# Revit family: Metal_Lockers-Salsbury_Industries-51000_Series-3_Wide_Units
name_source: partatom
category: Specialty Equipment
units: mm (PartAtom-declared; Revit-internal decimal feet)

## family parameters
Always vertical = Yes
Classification Number = 23.40.00.00
Cut with Voids When Loaded = No
Enable Cutting in Views = No
Maintain Annotation Orientation = No
Part Type = Normal
Room Calculation Point = No
Round Connector Dimension = Use Diameter
Shared = No
Work Plane-Based = No

## types (6) — shared parameters
Assembly Code = C1030310
Building Codes = https://www.lockers.com
Construction Details = https://www.lockers.com
Door Location D1 = Metal Locker Doors-15 inch with Hasps : Single Tier Door - 6 foot
Green Building-LEED = https://www.arcat.com
Hasp Handle Material = Plastic - Salsbury Finish - Black
Hasp Plate Rivet Material = Steel -Salsbury Finish - Polished Steel
Installation-Fabrication = https://www.lockers.com
Keynote = 10 51 00
Manufacturer = Salsbury Industries
Manufacturer Fax = 1-800-562-5399
Manufacturer Website = https://www.lockers.com
MasterFormat Number = 10 51 13
MasterFormat Title = Lockers
OmniClass 23 Number = 23.40.00.00
OmniClass 23 Title = Equipment and Furnishings
Product Data = https://www.lockers.com
Revision = R1_2018-10
Sales Information = https://www.lockers.com
Specification = https://www.lockers.com
Test Data = https://www.lockers.com
Type Comments = 15" Wide Standard Metal Lockers - Single Tier
URL = www.lockers.com
Unit Height = 72 "
Version = 2.0 (02/28/18)
Width = 45.04 "
zero-valued in all types: Default Elevation

## per-type parameters (varying)
| type | Base Height | Depth | Description | Model | Sloping Hood Height | Standard Leg Base | Zee Base |
| 51365 - with Standard 6" High Legs | 6 " | 15.01 " | 3 Wide - 6 Feet High - 15 Inches Deep | 51365 | 8.682 " | Metal Locker Legs - 3 Wide : 6" High - 45"W x 15"D | Metal Locker Zee Base - 3 Wide : None |
| 51368 - with Standard 6" High Legs | 6 " | 18.01 " | 3 Wide - 6 Feet High - 18 Inches Deep | 51368 | 10.739 " | Metal Locker Legs - 3 Wide : 6" High - 45"W x 18"D | Metal Locker Zee Base - 3 Wide : None |
| 51365 - with 77575 Zee Base and 77550 Lockers without Legs | 4 " | 15.01 " | 3 Wide - 6 Feet High - 15 Inches Deep with Zee Base and Lockers without Legs | 51365 with 77575 and 77550 | 8.682 " | Metal Locker Legs - 3 Wide : No Legs | Metal Locker Zee Base - 3 Wide : 77575 - 45"W x 15"D |
| 51368 - with 77578 Zee Base and 77550 Lockers without Legs | 4 " | 18.01 " | 3 Wide - 6 Feet High - 18 Inches Deep with Zee Base and Lockers without Legs | 51368 with 77578 and 77550 | 10.739 " | Metal Locker Legs - 3 Wide : No Legs | Metal Locker Zee Base - 3 Wide : 77578 - 45"W x 18"D |
| 51365 - with 77550 Lockers without Legs | 0 " | 15.01 " | 3 Wide - 6 Feet High - 15 Inches Deep with Lockers without Legs | 51365 with 77550 | 8.682 " | Metal Locker Legs - 3 Wide : No Legs | Metal Locker Zee Base - 3 Wide : None |
| 51368 - with 77550 Lockers without Legs | 0 " | 18.01 " | 3 Wide - 6 Feet High - 18 Inches Deep with Lockers without Legs | 51368 with 77550 | 10.739 " | Metal Locker Legs - 3 Wide : No Legs | Metal Locker Zee Base - 3 Wide : None |

## geometry (parser evidence)
native form markers: Sweep x39
no freeform markers — native parametric forms only
